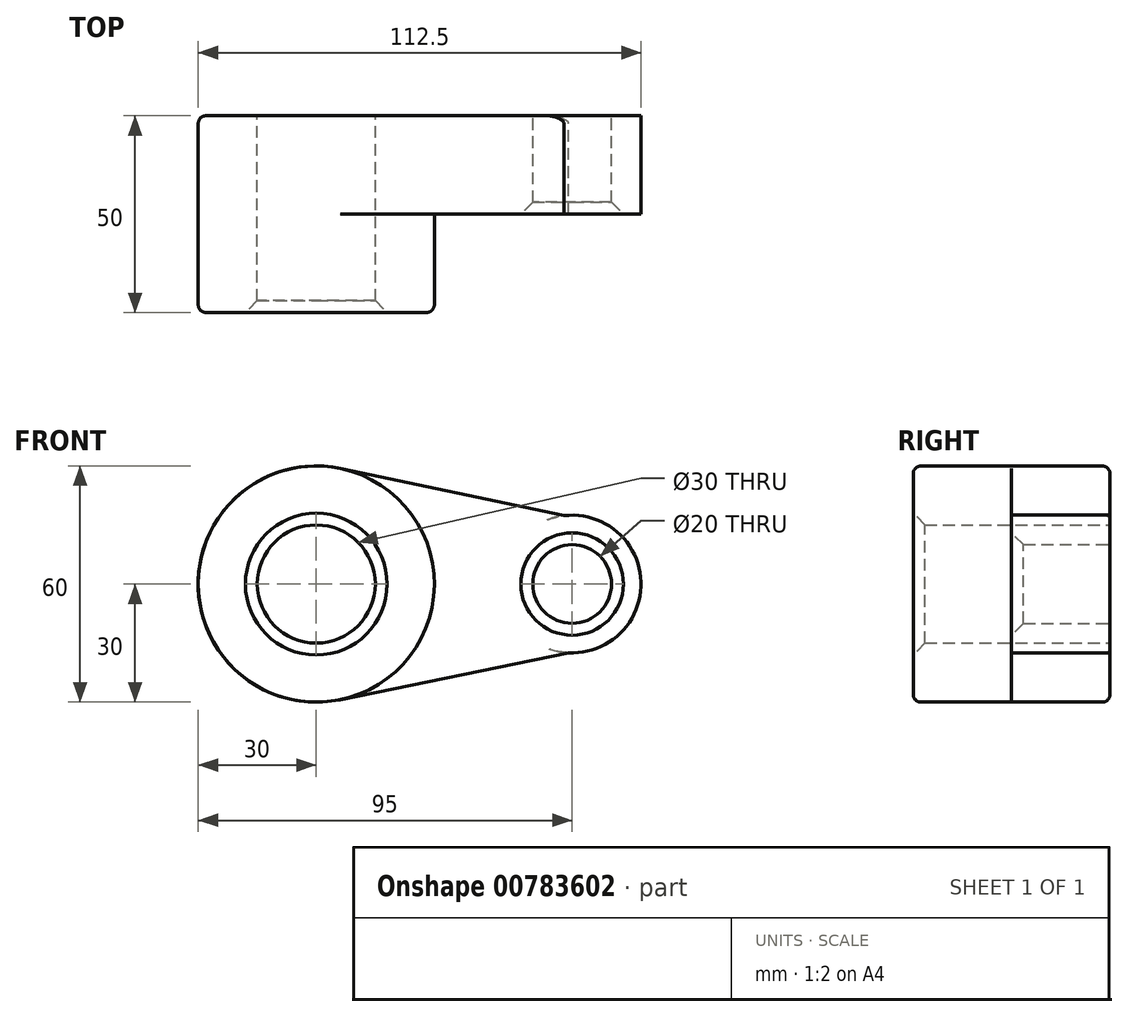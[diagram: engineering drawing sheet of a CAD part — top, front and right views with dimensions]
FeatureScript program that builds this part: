
annotation { "Feature Type Name" : "Feature", "Feature Type Description" : "" }
export const myFeature = defineFeature(function(context is Context, id is Id, definition is map)
    precondition{}
    {
        {
            var Q0;
            Q0=qCreatedBy(makeId("Front.planeOp"),FACE);
            var sketch = newSketch(context, id + "F0", { "sketchPlane" : qUnion([Q0])});
            skCircle(sketch, "E0", {"center": v(0, 0) * mm, "radius": 30 * mm});
            skCircle(sketch, "E1", {"center": v(65, 0) * mm, "radius": 17.5 * mm});
            skLineSegment(sketch, "E2", {"start": v(6.19, 29.36) * mm, "end": v(62.99, 17.38) * mm});
            skLineSegment(sketch, "E3", {"start": v(6.03, -29.39) * mm, "end": v(64.1, -17.48) * mm});
            skCircle(sketch, "E4", {"center": v(0, 0) * mm, "radius": 15 * mm});
            skCircle(sketch, "E5", {"center": v(65, 0) * mm, "radius": 10 * mm});
            skSolve(sketch);
        }
        {
            var Q0;
            Q0 = qSketchRegion(id + "F0", true);
            extrude(context, id + "F1", {"entities" : qUnion([Q0]), "depth" : 25 * mm, "offsetDistance" : 25 * mm});
        }
        {
            var Q0;
            Q0=makeQuery(id+"F0.imprint","IMPRINT",FACE,{"disambiguationData":[TD([[makeQuery(id+"F0.imprint","IMPRINT",EDGE,{"derivedFrom":sQuery(id+"F0.wireOp",EDGE,"E4")}),-1.0]])]});
            extrude(context, id + "F2", {"entities" : qUnion([Q0]), "operationType" : NewBodyOperationType.ADD, "depth" : 50 * mm, "offsetDistance" : 25 * mm});
        }
        {
            var Q0;
            Q0=makeQuery(id+"F2.opExtrude","CAP_EDGE",EDGE,{"disambiguationData":[OSD([sQuery(id+"F0.wireOp",EDGE,"E4")])],"isStart":false});
            var Q1;
            Q1=makeQuery(id+"F1.opExtrude","CAP_EDGE",EDGE,{"disambiguationData":[OSD([sQuery(id+"F0.wireOp",EDGE,"E5")])],"isStart":false});
            chamfer(context, id + "F3", {"entities" : qUnion([Q0, Q1]), "width" : 3 * mm, "tangentPropagation" : true});
        }
        {
            var Q0;
            Q0=makeQuery(id+"F2.opExtrude","CAP_EDGE",EDGE,{"disambiguationData":[OSD([sQuery(id+"F0.wireOp",EDGE,"E0")])],"isStart":false});
            var Q1;
            Q1=makeQuery(id+"F1.opExtrude","CAP_EDGE",EDGE,{"disambiguationData":[OSD([sQuery(id+"F0.wireOp",EDGE,"E3")])],"isStart":true});
            fillet(context, id + "F4", {"entities" : qUnion([Q0, Q1]), "radius" : 2 * mm, "tangentPropagation" : true, "allowEdgeOverflow" : false});
        }
    });
